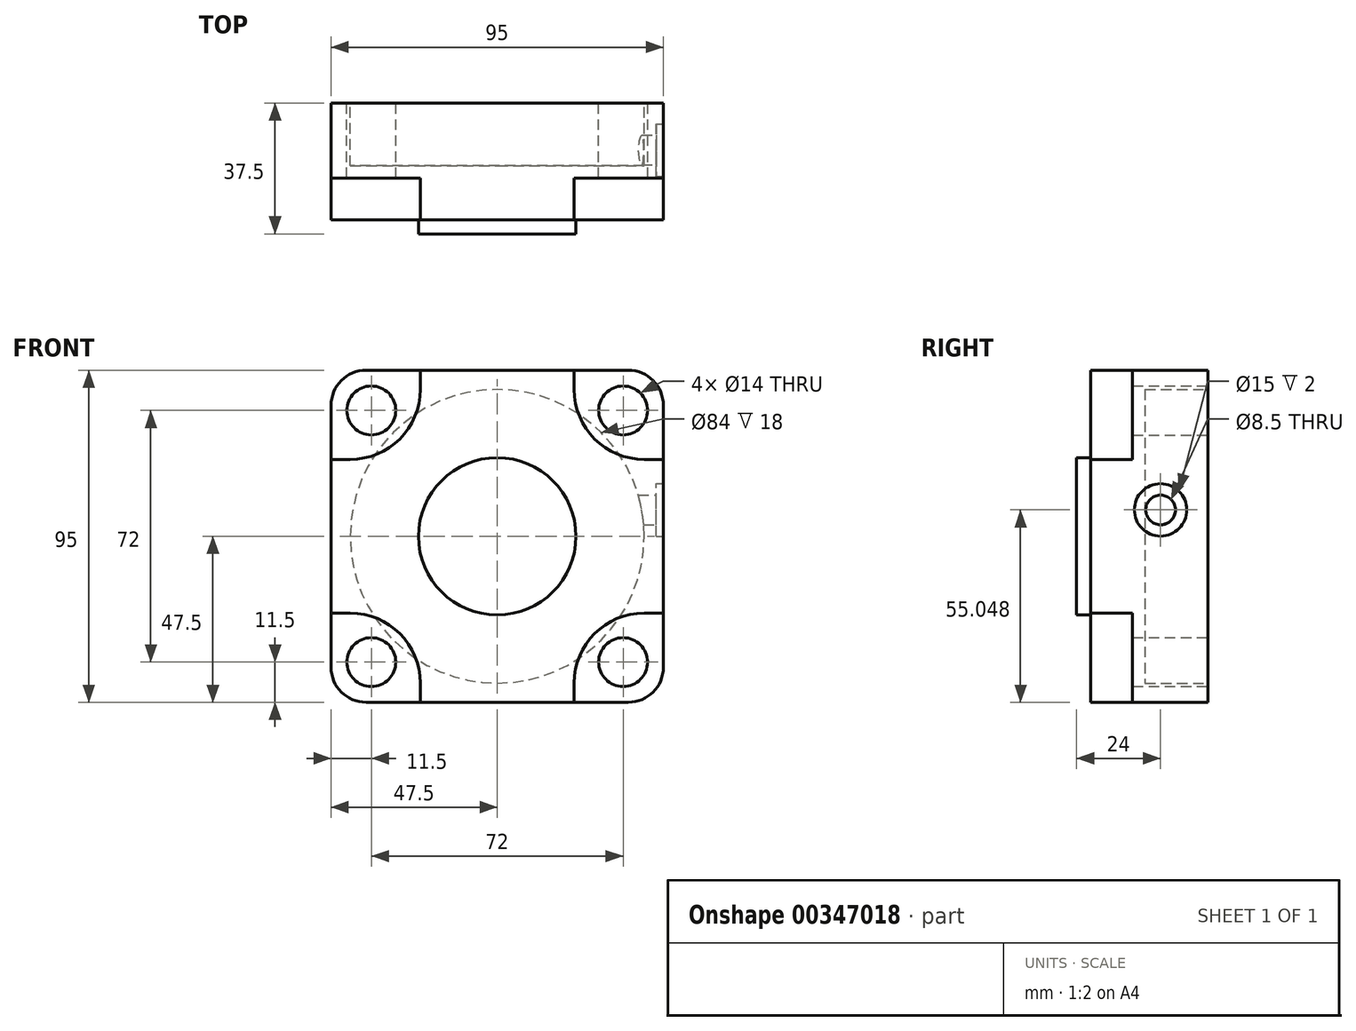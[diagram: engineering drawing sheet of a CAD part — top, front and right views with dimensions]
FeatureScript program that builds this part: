
annotation { "Feature Type Name" : "Feature", "Feature Type Description" : "" }
export const myFeature = defineFeature(function(context is Context, id is Id, definition is map)
    precondition{}
    {
        {
            var Q0;
            Q0=qCreatedBy(makeId("Front.planeOp"),FACE);
            var sketch = newSketch(context, id + "F0", { "sketchPlane" : qUnion([Q0])});
            skLineSegment(sketch, "E0.bottom", {"start": v(37.5, -47.5) * mm, "end": v(-37.5, -47.5) * mm});
            skLineSegment(sketch, "E0.top", {"start": v(37.5, 47.5) * mm, "end": v(-37.5, 47.5) * mm});
            skLineSegment(sketch, "E0.left", {"start": v(47.5, -37.5) * mm, "end": v(47.5, 37.5) * mm});
            skLineSegment(sketch, "E0.right", {"start": v(-47.5, -37.5) * mm, "end": v(-47.5, 37.5) * mm});
            skPoint(sketch, "E0.middle", {"position": v(0, 0) * mm});
            skPoint(sketch, "E1.visualSharp", {"position": v(-47.5, 47.5) * mm});
            skArc(sketch, "E1.filletArc", {"start": v(-37.5, 47.5) * mm, "mid": v(-44.57, 44.57) * mm, "end": v(-47.5, 37.5) * mm});
            skPoint(sketch, "E2.visualSharp", {"position": v(47.5, 47.5) * mm});
            skArc(sketch, "E2.filletArc", {"start": v(47.5, 37.5) * mm, "mid": v(44.57, 44.57) * mm, "end": v(37.5, 47.5) * mm});
            skPoint(sketch, "E3.visualSharp", {"position": v(47.5, -47.5) * mm});
            skArc(sketch, "E3.filletArc", {"start": v(37.5, -47.5) * mm, "mid": v(44.57, -44.57) * mm, "end": v(47.5, -37.5) * mm});
            skPoint(sketch, "E4.visualSharp", {"position": v(-47.5, -47.5) * mm});
            skArc(sketch, "E4.filletArc", {"start": v(-47.5, -37.5) * mm, "mid": v(-44.57, -44.57) * mm, "end": v(-37.5, -47.5) * mm});
            skLineSegment(sketch, "E5", {"start": v(0, 47.5) * mm, "end": v(0, -47.5) * mm, "construction": true});
            skLineSegment(sketch, "E6.0", {"start": v(-36, 47.5) * mm, "end": v(-36, -47.5) * mm, "construction": true});
            skLineSegment(sketch, "E7.0", {"start": v(36, 47.5) * mm, "end": v(36, -47.5) * mm, "construction": true});
            skLineSegment(sketch, "E8", {"start": v(-47.5, 0) * mm, "end": v(47.5, 0) * mm, "construction": true});
            skLineSegment(sketch, "E9.0", {"start": v(-47.5, -36) * mm, "end": v(47.5, -36) * mm, "construction": true});
            skLineSegment(sketch, "E10.0", {"start": v(-47.5, 36) * mm, "end": v(47.5, 36) * mm, "construction": true});
            skCircle(sketch, "E11", {"center": v(-36, 36) * mm, "radius": 7 * mm});
            skCircle(sketch, "E12", {"center": v(36, 36) * mm, "radius": 7 * mm});
            skCircle(sketch, "E13", {"center": v(-36, -36) * mm, "radius": 7 * mm});
            skCircle(sketch, "E14", {"center": v(36, -36) * mm, "radius": 7 * mm});
            skSolve(sketch);
        }
        {
            var Q0;
            Q0=makeQuery(id+"F0.imprint","IMPRINT",FACE,{"disambiguationData":[TD([[makeQuery(id+"F0.imprint","IMPRINT",EDGE,{"derivedFrom":sQuery(id+"F0.wireOp",EDGE,"E0.bottom")}),-1.0]])]});
            extrude(context, id + "F1", {"entities" : qUnion([Q0]), "endBound" : BoundingType.SYMMETRIC, "depth" : 33.5 * mm});
        }
        {
            var Q0;
            Q0=makeQuery(id+"F1.opExtrude","CAP_FACE",FACE,{"disambiguationData":[OSD([sQuery(id+"F0.wireOp",EDGE,"E0.bottom"),sQuery(id+"F0.wireOp",EDGE,"E0.top"),sQuery(id+"F0.wireOp",EDGE,"E0.left"),sQuery(id+"F0.wireOp",EDGE,"E0.right"),sQuery(id+"F0.wireOp",EDGE,"E1.filletArc"),sQuery(id+"F0.wireOp",EDGE,"E2.filletArc"),sQuery(id+"F0.wireOp",EDGE,"E3.filletArc"),sQuery(id+"F0.wireOp",EDGE,"E4.filletArc"),sQuery(id+"F0.wireOp",EDGE,"E11"),sQuery(id+"F0.wireOp",EDGE,"E12"),sQuery(id+"F0.wireOp",EDGE,"E13"),sQuery(id+"F0.wireOp",EDGE,"E14")])],"isStart":false});
            var sketch = newSketch(context, id + "F2", { "sketchPlane" : qUnion([Q0])});
            skLineSegment(sketch, "E15", {"start": v(-47.5, 22) * mm, "end": v(-42, 22) * mm});
            skLineSegment(sketch, "E16", {"start": v(-47.5, -22) * mm, "end": v(-42, -22) * mm});
            skLineSegment(sketch, "E17", {"start": v(-22, 47.5) * mm, "end": v(-22, 42) * mm});
            skLineSegment(sketch, "E18", {"start": v(22, 47.5) * mm, "end": v(22, 42) * mm});
            skLineSegment(sketch, "E19", {"start": v(42, 22) * mm, "end": v(47.5, 22) * mm});
            skLineSegment(sketch, "E20", {"start": v(42, -22) * mm, "end": v(47.5, -22) * mm});
            skLineSegment(sketch, "E21", {"start": v(22, -42) * mm, "end": v(22, -47.5) * mm});
            skLineSegment(sketch, "E22", {"start": v(-22, -42) * mm, "end": v(-22, -47.5) * mm});
            skArc(sketch, "E23.filletArc", {"start": v(-42, 22) * mm, "mid": v(-27.86, 27.86) * mm, "end": v(-22, 42) * mm});
            skPoint(sketch, "E24.newPointA", {"position": v(0.48, 22) * mm});
            skArc(sketch, "E24.filletArc", {"start": v(22, 42) * mm, "mid": v(27.86, 27.86) * mm, "end": v(42, 22) * mm});
            skPoint(sketch, "E25.newPointB", {"position": v(-22, -0.08) * mm});
            skArc(sketch, "E25.filletArc", {"start": v(-22, -42) * mm, "mid": v(-27.86, -27.86) * mm, "end": v(-42, -22) * mm});
            skPoint(sketch, "E26.newPointA", {"position": v(1.13, -22) * mm});
            skPoint(sketch, "E26.newPointB", {"position": v(22, -0.08) * mm});
            skArc(sketch, "E26.filletArc", {"start": v(42, -22) * mm, "mid": v(27.86, -27.86) * mm, "end": v(22, -42) * mm});
            skLineSegment(sketch, "E27.0", {"start": v(-47.5, -37.5) * mm, "end": v(-47.5, -22) * mm});
            skArc(sketch, "E28.0", {"start": v(-37.5, 47.5) * mm, "mid": v(-44.57, 44.57) * mm, "end": v(-47.5, 37.5) * mm});
            skLineSegment(sketch, "E29.0", {"start": v(37.5, 47.5) * mm, "end": v(22, 47.5) * mm});
            skPoint(sketch, "E30.0", {"position": v(44.57, 44.57) * mm});
            skArc(sketch, "E31.0", {"start": v(47.5, 37.5) * mm, "mid": v(44.57, 44.57) * mm, "end": v(37.5, 47.5) * mm});
            skLineSegment(sketch, "E32.0", {"start": v(47.5, -37.5) * mm, "end": v(47.5, -22) * mm});
            skPoint(sketch, "E33.0", {"position": v(44.57, -44.57) * mm});
            skArc(sketch, "E34.0", {"start": v(37.5, -47.5) * mm, "mid": v(44.57, -44.57) * mm, "end": v(47.5, -37.5) * mm});
            skLineSegment(sketch, "E35.0", {"start": v(37.5, -47.5) * mm, "end": v(22, -47.5) * mm});
            skArc(sketch, "E36.0", {"start": v(-47.5, -37.5) * mm, "mid": v(-44.57, -44.57) * mm, "end": v(-37.5, -47.5) * mm});
            skPoint(sketch, "E37.orphan", {"position": v(-51.1, 22) * mm});
            skPoint(sketch, "E38.orphan", {"position": v(-22, 52.95) * mm});
            skLineSegment(sketch, "E39.trimOffspring", {"start": v(-22, 47.5) * mm, "end": v(-37.5, 47.5) * mm});
            skLineSegment(sketch, "E40.trimOffspring", {"start": v(-47.5, 22) * mm, "end": v(-47.5, 37.5) * mm});
            skPoint(sketch, "E41.orphan", {"position": v(-22, -53.12) * mm});
            skPoint(sketch, "E42.orphan", {"position": v(-51.1, -22) * mm});
            skLineSegment(sketch, "E43.trimOffspring", {"start": v(-22, -47.5) * mm, "end": v(-37.5, -47.5) * mm});
            skPoint(sketch, "E44.orphan", {"position": v(22, -51.66) * mm});
            skPoint(sketch, "E45.orphan", {"position": v(53.36, -22) * mm});
            skPoint(sketch, "E46.orphan", {"position": v(52.07, 22) * mm});
            skPoint(sketch, "E47.orphan", {"position": v(22, 51.5) * mm});
            skLineSegment(sketch, "E48.trimOffspring", {"start": v(47.5, 22) * mm, "end": v(47.5, 37.5) * mm});
            skSolve(sketch);
        }
        {
            var Q0;
            Q0=makeQuery(id+"F2.imprint","IMPRINT",FACE,{"disambiguationData":[TD([[makeQuery(id+"F2.imprint","IMPRINT",EDGE,{"derivedFrom":sQuery(id+"F2.wireOp",EDGE,"E20")}),-1.0]])]});
            var Q1;
            Q1=makeQuery(id+"F2.imprint","IMPRINT",FACE,{"disambiguationData":[TD([[makeQuery(id+"F2.imprint","IMPRINT",EDGE,{"derivedFrom":sQuery(id+"F2.wireOp",EDGE,"E18")}),1.0]])]});
            var Q2;
            Q2=makeQuery(id+"F2.imprint","IMPRINT",FACE,{"disambiguationData":[TD([[makeQuery(id+"F2.imprint","IMPRINT",EDGE,{"derivedFrom":sQuery(id+"F2.wireOp",EDGE,"E15")}),1.0]])]});
            var Q3;
            Q3=makeQuery(id+"F2.imprint","IMPRINT",FACE,{"disambiguationData":[TD([[makeQuery(id+"F2.imprint","IMPRINT",EDGE,{"derivedFrom":sQuery(id+"F2.wireOp",EDGE,"E16")}),-1.0]])]});
            extrude(context, id + "F3", {"entities" : qUnion([Q0, Q1, Q2, Q3]), "operationType" : NewBodyOperationType.REMOVE, "oppositeDirection" : true, "depth" : 12 * mm});
        }
        {
            var Q0;
            Q0=makeQuery(id+"F1.opExtrude","CAP_FACE",FACE,{"disambiguationData":[OSD([sQuery(id+"F0.wireOp",EDGE,"E0.bottom"),sQuery(id+"F0.wireOp",EDGE,"E0.top"),sQuery(id+"F0.wireOp",EDGE,"E0.left"),sQuery(id+"F0.wireOp",EDGE,"E0.right"),sQuery(id+"F0.wireOp",EDGE,"E1.filletArc"),sQuery(id+"F0.wireOp",EDGE,"E2.filletArc"),sQuery(id+"F0.wireOp",EDGE,"E3.filletArc"),sQuery(id+"F0.wireOp",EDGE,"E4.filletArc"),sQuery(id+"F0.wireOp",EDGE,"E11"),sQuery(id+"F0.wireOp",EDGE,"E12"),sQuery(id+"F0.wireOp",EDGE,"E13"),sQuery(id+"F0.wireOp",EDGE,"E14")])],"isStart":false});
            var sketch = newSketch(context, id + "F4", { "sketchPlane" : qUnion([Q0])});
            skCircle(sketch, "E49", {"center": v(0, 0) * mm, "radius": 22.5 * mm});
            skSolve(sketch);
        }
        {
            var Q0;
            Q0=makeQuery(id+"F4.imprint","IMPRINT",FACE,{"disambiguationData":[TD([[makeQuery(id+"F4.imprint","IMPRINT",EDGE,{"derivedFrom":sQuery(id+"F4.wireOp",EDGE,"E49")}),1.0]])]});
            extrude(context, id + "F5", {"entities" : qUnion([Q0]), "operationType" : NewBodyOperationType.ADD, "depth" : 4 * mm});
        }
        {
            var Q0;
            Q0=makeQuery(id+"F1.opExtrude","CAP_FACE",FACE,{"disambiguationData":[OSD([sQuery(id+"F0.wireOp",EDGE,"E0.bottom"),sQuery(id+"F0.wireOp",EDGE,"E0.top"),sQuery(id+"F0.wireOp",EDGE,"E0.left"),sQuery(id+"F0.wireOp",EDGE,"E0.right"),sQuery(id+"F0.wireOp",EDGE,"E1.filletArc"),sQuery(id+"F0.wireOp",EDGE,"E2.filletArc"),sQuery(id+"F0.wireOp",EDGE,"E3.filletArc"),sQuery(id+"F0.wireOp",EDGE,"E4.filletArc"),sQuery(id+"F0.wireOp",EDGE,"E11"),sQuery(id+"F0.wireOp",EDGE,"E12"),sQuery(id+"F0.wireOp",EDGE,"E13"),sQuery(id+"F0.wireOp",EDGE,"E14")])],"isStart":true});
            var sketch = newSketch(context, id + "F6", { "sketchPlane" : qUnion([Q0])});
            skCircle(sketch, "E50", {"center": v(0, 0) * mm, "radius": 42 * mm});
            skSolve(sketch);
        }
        {
            var Q0;
            Q0=makeQuery(id+"F1.opExtrude","SWEPT_FACE",FACE,{"disambiguationData":[OSD([sQuery(id+"F0.wireOp",EDGE,"E0.left")])]});
            var sketch = newSketch(context, id + "F7", { "sketchPlane" : qUnion([Q0])});
            skLineSegment(sketch, "E51", {"start": v(3.25, 48.9) * mm, "end": v(3.25, -49.62) * mm, "construction": true});
            skCircle(sketch, "E52", {"center": v(3.25, 7.55) * mm, "radius": 4.25 * mm});
            skCircle(sketch, "E53", {"center": v(3.25, 7.55) * mm, "radius": 7.5 * mm});
            skSolve(sketch);
        }
        {
            var Q0;
            Q0=makeQuery(id+"F6.imprint","IMPRINT",FACE,{"disambiguationData":[TD([[makeQuery(id+"F6.imprint","IMPRINT",EDGE,{"derivedFrom":sQuery(id+"F6.wireOp",EDGE,"E50")}),1.0]])]});
            extrude(context, id + "F8", {"entities" : qUnion([Q0]), "operationType" : NewBodyOperationType.REMOVE, "oppositeDirection" : true, "depth" : 18 * mm});
        }
        {
            var Q0;
            Q0=makeQuery(id+"F7.imprint","IMPRINT",FACE,{"disambiguationData":[TD([[makeQuery(id+"F7.imprint","IMPRINT",EDGE,{"derivedFrom":sQuery(id+"F7.wireOp",EDGE,"E52")}),-1.0]])]});
            extrude(context, id + "F9", {"entities" : qUnion([Q0]), "operationType" : NewBodyOperationType.REMOVE, "oppositeDirection" : true, "depth" : 2 * mm});
        }
        {
            var Q0;
            Q0=makeQuery(id+"F9.boolean.opBoolean","SPLIT",FACE,{"disambiguationData":[TD([makeQuery(id+"F9.opExtrude","SWEPT_FACE",FACE,{"disambiguationData":[OSD([sQuery(id+"F7.wireOp",EDGE,"E52")])]})])],"derivedFrom":makeQuery(id+"F1.opExtrude","SWEPT_FACE",FACE,{"disambiguationData":[OSD([sQuery(id+"F0.wireOp",EDGE,"E0.left")])]})});
            extrude(context, id + "F10", {"entities" : qUnion([Q0]), "operationType" : NewBodyOperationType.REMOVE, "oppositeDirection" : true, "depth" : 8 * mm});
        }
    });
